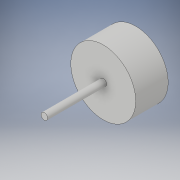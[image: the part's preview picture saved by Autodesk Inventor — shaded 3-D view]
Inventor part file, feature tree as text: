
AUTODESK INVENTOR PART (.ipt)
format: ipt  version: 2018.2 (Build 222227000, 227)  size: 98,304 bytes
history: native  units: in
note: dims shown in document units (in); Inventor stores cm internally (conversion verified against a paired STEP export)
features: extrude x2, sketch x2
ambient origin geometry x8: Origin, YZ Plane, XZ Plane, XY Plane, X Axis, Y Axis, Z Axis, Center Point
bodies: Solid1 (feature_tree)
feature tree (4):
  extrude  "Extrusion1"  Depth=0.8661in TaperAngle=0.0deg
  extrude  "Extrusion2"  Depth=1.5748in TaperAngle=0.0deg
  sketch  "Sketch1"  dims[d0=1.7323in d1=0.8661in d2=0.0in]
  sketch  "Sketch2"  dims[d3=0.1772in d4=1.5748in d5=0.0in]
